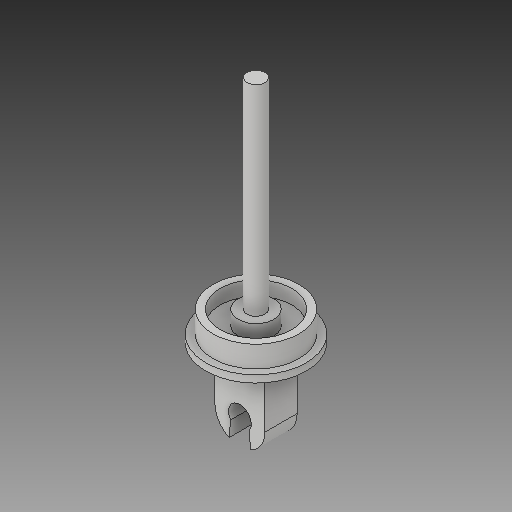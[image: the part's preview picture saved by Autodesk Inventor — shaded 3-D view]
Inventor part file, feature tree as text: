
AUTODESK INVENTOR PART (.ipt)
format: ipt  version: 2019 (Build 230136000, 136)  size: 138,752 bytes
history: native  units: in
note: dims shown in document units (in); Inventor stores cm internally (conversion verified against a paired STEP export)
features: sketch x5, other x3
ambient origin geometry x8: Origin, YZ Plane, XZ Plane, XY Plane, X Axis, Y Axis, Z Axis, Center Point
bodies: Solid1 (feature_tree)
feature tree (8):
  other  "Bottom.ipt"
  other  "Solid1::Bottom.ipt"
  other  "TaggingFeature1"
  sketch  "Sketch1"  dims[d0=0.3937in]
  sketch  "Sketch2"
  sketch  "Sketch3"
  sketch  "Sketch4"
  sketch  "Sketch5"
